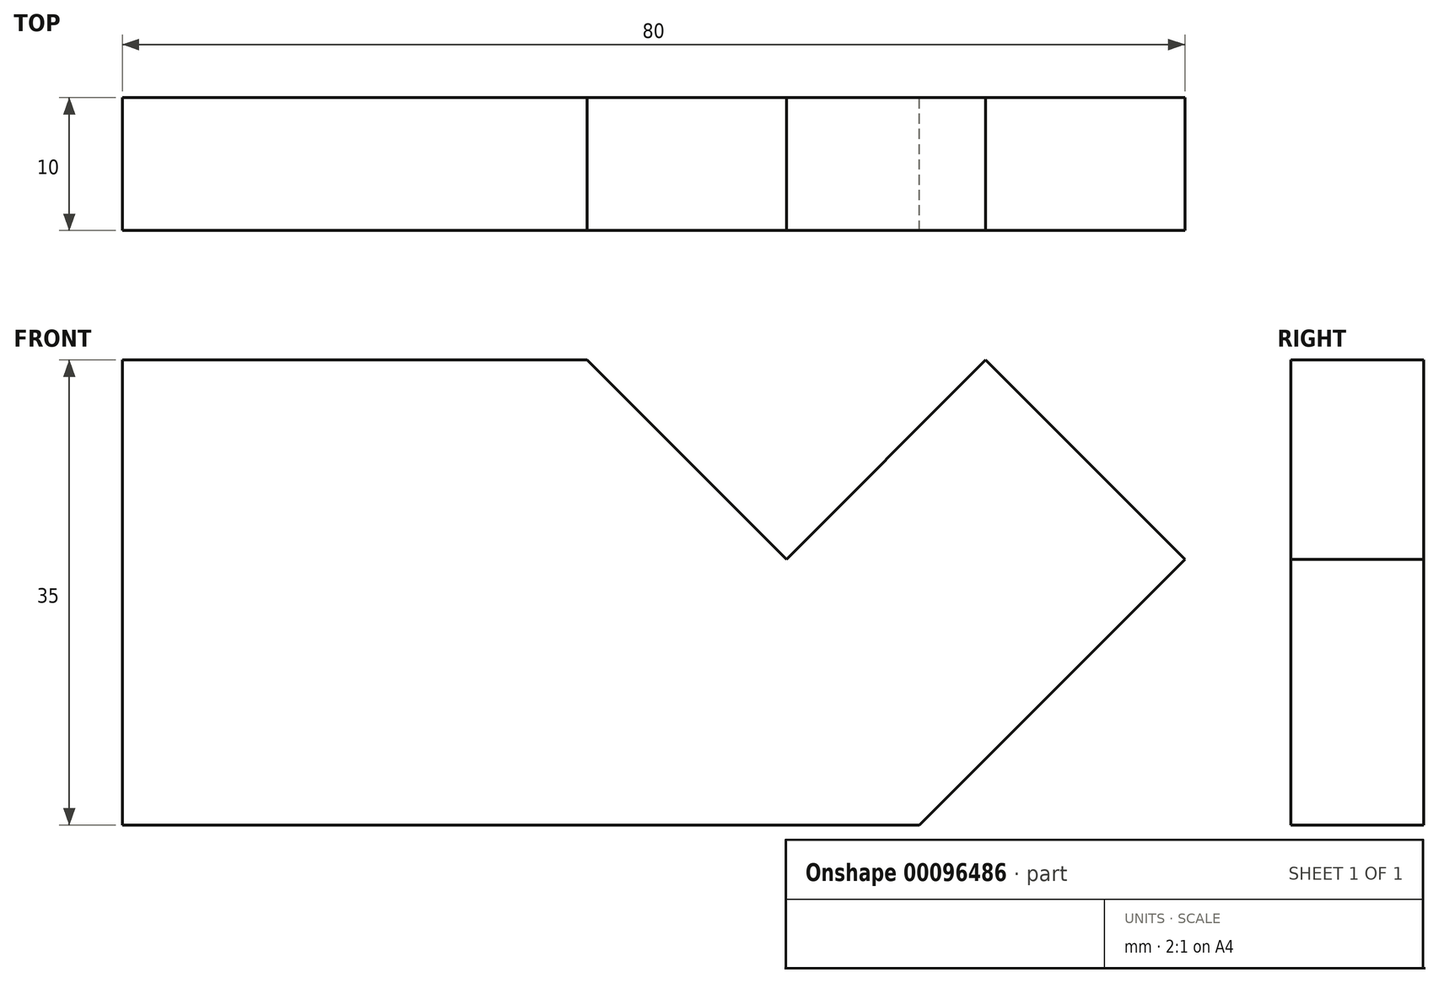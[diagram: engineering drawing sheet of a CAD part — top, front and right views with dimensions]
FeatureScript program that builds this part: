
annotation { "Feature Type Name" : "Feature", "Feature Type Description" : "" }
export const myFeature = defineFeature(function(context is Context, id is Id, definition is map)
    precondition{}
    {
        {
            var Q0;
            Q0=qCreatedBy(makeId("Front.planeOp"),FACE);
            var sketch = newSketch(context, id + "F0", { "sketchPlane" : qUnion([Q0])});
            skLineSegment(sketch, "E0.bottom", {"start": v(0, 0) * mm, "end": v(80, 0) * mm, "construction": true});
            skLineSegment(sketch, "E0.top", {"start": v(0, 35) * mm, "end": v(80, 35) * mm, "construction": true});
            skLineSegment(sketch, "E0.left", {"start": v(0, 0) * mm, "end": v(0, 35) * mm, "construction": true});
            skLineSegment(sketch, "E0.right", {"start": v(80, 0) * mm, "end": v(80, 35) * mm, "construction": true});
            skLineSegment(sketch, "E1", {"start": v(0, 0) * mm, "end": v(0, 35) * mm});
            skLineSegment(sketch, "E2", {"start": v(0, 35) * mm, "end": v(35, 35) * mm});
            skLineSegment(sketch, "E3", {"start": v(35, 35) * mm, "end": v(50, 20) * mm});
            skLineSegment(sketch, "E4", {"start": v(50, 20) * mm, "end": v(65, 35) * mm});
            skLineSegment(sketch, "E5", {"start": v(65, 35) * mm, "end": v(80, 20) * mm});
            skLineSegment(sketch, "E6", {"start": v(80, 20) * mm, "end": v(60, 0) * mm});
            skLineSegment(sketch, "E7", {"start": v(60, 0) * mm, "end": v(0, 0) * mm});
            skSolve(sketch);
        }
        {
            var Q0;
            Q0=makeQuery(id+"F0.imprint","IMPRINT",FACE,{"disambiguationData":[TD([[makeQuery(id+"F0.imprint","IMPRINT",EDGE,{"derivedFrom":sQuery(id+"F0.wireOp",EDGE,"E1")}),-1.0]])]});
            extrude(context, id + "F1", {"entities" : qUnion([Q0]), "depth" : 10 * mm});
        }
    });
